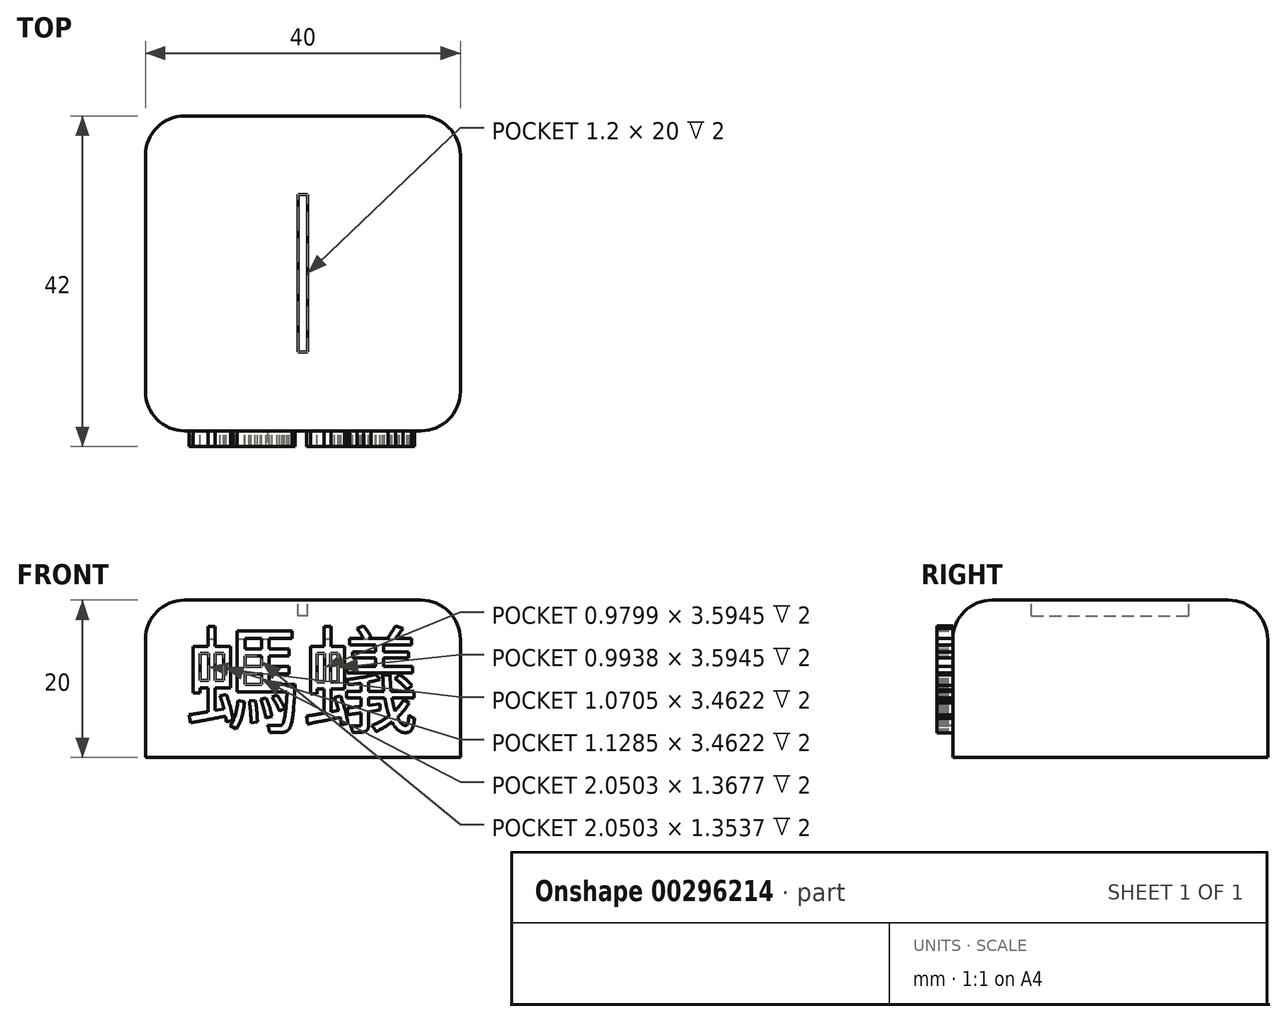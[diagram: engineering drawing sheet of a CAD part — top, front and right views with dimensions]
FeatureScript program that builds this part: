
annotation { "Feature Type Name" : "Feature", "Feature Type Description" : "" }
export const myFeature = defineFeature(function(context is Context, id is Id, definition is map)
    precondition{}
    {
        {
            var Q0;
            Q0=qCreatedBy(makeId("Top.planeOp"),FACE);
            var sketch = newSketch(context, id + "F0", { "sketchPlane" : qUnion([Q0])});
            skLineSegment(sketch, "E0.bottom", {"start": v(20, -20) * mm, "end": v(-20, -20) * mm});
            skLineSegment(sketch, "E0.top", {"start": v(20, 20) * mm, "end": v(-20, 20) * mm});
            skLineSegment(sketch, "E0.left", {"start": v(20, -20) * mm, "end": v(20, 20) * mm});
            skLineSegment(sketch, "E0.right", {"start": v(-20, -20) * mm, "end": v(-20, 20) * mm});
            skPoint(sketch, "E0.middle", {"position": v(0, 0) * mm});
            skLineSegment(sketch, "E1.bottom", {"start": v(0.6, -10) * mm, "end": v(-0.6, -10) * mm});
            skLineSegment(sketch, "E1.top", {"start": v(0.6, 10) * mm, "end": v(-0.6, 10) * mm});
            skLineSegment(sketch, "E1.left", {"start": v(0.6, -10) * mm, "end": v(0.6, 10) * mm});
            skLineSegment(sketch, "E1.right", {"start": v(-0.6, -10) * mm, "end": v(-0.6, 10) * mm});
            skSolve(sketch);
        }
        {
            var Q0;
            Q0=makeQuery(id+"F0.imprint","IMPRINT",FACE,{"disambiguationData":[TD([[makeQuery(id+"F0.imprint","IMPRINT",EDGE,{"derivedFrom":sQuery(id+"F0.wireOp",EDGE,"E0.bottom")}),-1.0]])]});
            var Q1;
            Q1=makeQuery(id+"F0.imprint","IMPRINT",FACE,{"disambiguationData":[TD([[makeQuery(id+"F0.imprint","IMPRINT",EDGE,{"derivedFrom":sQuery(id+"F0.wireOp",EDGE,"E1.bottom")}),-1.0]])]});
            extrude(context, id + "F1", {"entities" : qUnion([Q0, Q1]), "oppositeDirection" : true, "depth" : 20 * mm});
        }
        {
            var Q0;
            Q0=makeQuery(id+"F0.imprint","IMPRINT",FACE,{"disambiguationData":[TD([[makeQuery(id+"F0.imprint","IMPRINT",EDGE,{"derivedFrom":sQuery(id+"F0.wireOp",EDGE,"E1.bottom")}),-1.0]])]});
            extrude(context, id + "F2", {"entities" : qUnion([Q0]), "operationType" : NewBodyOperationType.REMOVE, "oppositeDirection" : true, "depth" : 2 * mm});
        }
        {
            var Q0;
            Q0=makeQuery(id+"F2.boolean.opBoolean","COPY",EDGE,{"derivedFrom":makeQuery(id+"F2.opExtrude","CAP_EDGE",EDGE,{"disambiguationData":[OSD([sQuery(id+"F0.wireOp",EDGE,"E1.left")])],"isStart":true})});
            var Q1;
            Q1=makeQuery(id+"F2.boolean.opBoolean","COPY",EDGE,{"derivedFrom":makeQuery(id+"F2.opExtrude","CAP_EDGE",EDGE,{"disambiguationData":[OSD([sQuery(id+"F0.wireOp",EDGE,"E1.right")])],"isStart":true})});
            var Q2;
            Q2=makeQuery(id+"F1.opExtrude","SWEPT_EDGE",EDGE,{"disambiguationData":[OSD([sQuery(id+"F0.wireOp",EDGE,"E0.bottom"),sQuery(id+"F0.wireOp",EDGE,"E0.left")])]});
            var Q3;
            Q3=makeQuery(id+"F1.opExtrude","SWEPT_EDGE",EDGE,{"disambiguationData":[OSD([sQuery(id+"F0.wireOp",EDGE,"E0.top"),sQuery(id+"F0.wireOp",EDGE,"E0.left")])]});
            var Q4;
            Q4=makeQuery(id+"F1.opExtrude","CAP_EDGE",EDGE,{"disambiguationData":[OSD([sQuery(id+"F0.wireOp",EDGE,"E0.left")])],"isStart":true});
            var Q5;
            Q5=makeQuery(id+"F1.opExtrude","SWEPT_EDGE",EDGE,{"disambiguationData":[OSD([sQuery(id+"F0.wireOp",EDGE,"E0.bottom"),sQuery(id+"F0.wireOp",EDGE,"E0.right")])]});
            var Q6;
            Q6=makeQuery(id+"F1.opExtrude","SWEPT_EDGE",EDGE,{"disambiguationData":[OSD([sQuery(id+"F0.wireOp",EDGE,"E0.top"),sQuery(id+"F0.wireOp",EDGE,"E0.right")])]});
            var Q7;
            Q7=makeQuery(id+"F1.opExtrude","CAP_EDGE",EDGE,{"disambiguationData":[OSD([sQuery(id+"F0.wireOp",EDGE,"E0.top")])],"isStart":true});
            var Q8;
            Q8=makeQuery(id+"F1.opExtrude","CAP_EDGE",EDGE,{"disambiguationData":[OSD([sQuery(id+"F0.wireOp",EDGE,"E0.right")])],"isStart":true});
            var Q9;
            Q9=makeQuery(id+"F1.opExtrude","CAP_EDGE",EDGE,{"disambiguationData":[OSD([sQuery(id+"F0.wireOp",EDGE,"E0.bottom")])],"isStart":true});
            fillet(context, id + "F3", {"entities" : qUnion([Q0, Q1, Q2, Q3, Q4, Q5, Q6, Q7, Q8, Q9]), "radius" : 5 * mm, "tangentPropagation" : true, "allowEdgeOverflow" : false});
        }
        {
            var Q0;
            Q0=makeQuery(id+"F1.opExtrude","SWEPT_FACE",FACE,{"disambiguationData":[OSD([sQuery(id+"F0.wireOp",EDGE,"E0.bottom")])]});
            var sketch = newSketch(context, id + "F4", { "sketchPlane" : qUnion([Q0])});
            skText(sketch, "E2", { "text": "螞蟻", "fontName": "NotoSansCJKtc-Regular.otf"});
            const initialGuessF4  = {"E2": [-0.015, -0.0157, 1, 0, 0.0107]};
            skSetInitialGuess(sketch, initialGuessF4);
            skSolve(sketch);
        }
        {
            var Q0;
            Q0=makeQuery(id+"F4.imprint","IMPRINT",FACE,{"disambiguationData":[TD([[makeQuery(id+"F4.imprint","IMPRINT",EDGE,{"derivedFrom":sQuery(id+"F4.wireOp",EDGE,"E2.sketch_text.stroke-111")}),1.0]])]});
            var Q1;
            {var subQ0=sQuery(id+"F4.wireOp",EDGE,"E2.sketch_text.stroke-89");Q1=makeQuery(id+"F4.imprint","IMPRINT",FACE,{"disambiguationData":[TD([[makeQuery(id+"F4.imprint","IMPRINT",EDGE,{"derivedFrom":subQ0}),1.0]])]});}
            var Q2;
            Q2=makeQuery(id+"F4.imprint","IMPRINT",FACE,{"disambiguationData":[TD([[makeQuery(id+"F4.imprint","IMPRINT",EDGE,{"derivedFrom":sQuery(id+"F4.wireOp",EDGE,"E2.sketch_text.stroke-81")}),1.0]])]});
            var Q3;
            Q3=makeQuery(id+"F4.imprint","IMPRINT",FACE,{"disambiguationData":[TD([[makeQuery(id+"F4.imprint","IMPRINT",EDGE,{"derivedFrom":sQuery(id+"F4.wireOp",EDGE,"E2.sketch_text.stroke-145")}),1.0]])]});
            var Q4;
            Q4=makeQuery(id+"F4.imprint","IMPRINT",FACE,{"disambiguationData":[TD([[makeQuery(id+"F4.imprint","IMPRINT",EDGE,{"derivedFrom":sQuery(id+"F4.wireOp",EDGE,"E2.sketch_text.stroke-115")}),1.0]])]});
            var Q5;
            {var subQ0=sQuery(id+"F4.wireOp",EDGE,"E2.sketch_text.stroke-130");Q5=makeQuery(id+"F4.imprint","IMPRINT",FACE,{"disambiguationData":[TD([[makeQuery(id+"F4.imprint","IMPRINT",EDGE,{"derivedFrom":subQ0}),1.0]])]});}
            var Q6;
            {var subQ7=sQuery(id+"F4.wireOp",EDGE,"E2.sketch_text.stroke-49");Q6=makeQuery(id+"F4.imprint","IMPRINT",FACE,{"disambiguationData":[TD([[makeQuery(id+"F4.imprint","IMPRINT",EDGE,{"derivedFrom":subQ7}),1.0]])]});}
            var Q7;
            {var subQ0=sQuery(id+"F4.wireOp",EDGE,"E2.sketch_text.stroke-17");Q7=makeQuery(id+"F4.imprint","IMPRINT",FACE,{"disambiguationData":[TD([[makeQuery(id+"F4.imprint","IMPRINT",EDGE,{"derivedFrom":subQ0}),1.0]])]});}
            extrude(context, id + "F5", {"entities" : qUnion([Q0, Q1, Q2, Q3, Q4, Q5, Q6, Q7]), "operationType" : NewBodyOperationType.ADD, "depth" : 2 * mm});
        }
        {
            var Q0;
            Q0=makeQuery(id+"F4.imprint","IMPRINT",FACE,{"disambiguationData":[TD([[makeQuery(id+"F4.imprint","IMPRINT",EDGE,{"derivedFrom":sQuery(id+"F4.wireOp",EDGE,"E2.sketch_text.stroke-0")}),1.0]])]});
            var Q1;
            Q1=makeQuery(id+"F4.imprint","IMPRINT",FACE,{"disambiguationData":[TD([[makeQuery(id+"F4.imprint","IMPRINT",EDGE,{"derivedFrom":sQuery(id+"F4.wireOp",EDGE,"E2.sketch_text.stroke-42")}),1.0]])]});
            var Q2;
            Q2=makeQuery(id+"F4.imprint","IMPRINT",FACE,{"disambiguationData":[TD([[makeQuery(id+"F4.imprint","IMPRINT",EDGE,{"derivedFrom":sQuery(id+"F4.wireOp",EDGE,"E2.sketch_text.stroke-30")}),1.0]])]});
            var Q3;
            Q3=makeQuery(id+"F4.imprint","IMPRINT",FACE,{"disambiguationData":[TD([[makeQuery(id+"F4.imprint","IMPRINT",EDGE,{"derivedFrom":sQuery(id+"F4.wireOp",EDGE,"E2.sketch_text.stroke-34")}),1.0]])]});
            var Q4;
            Q4=makeQuery(id+"F4.imprint","IMPRINT",FACE,{"disambiguationData":[TD([[makeQuery(id+"F4.imprint","IMPRINT",EDGE,{"derivedFrom":sQuery(id+"F4.wireOp",EDGE,"E2.sketch_text.stroke-38")}),1.0]])]});
            var Q5;
            Q5=makeQuery(id+"F4.imprint","IMPRINT",FACE,{"disambiguationData":[TD([[makeQuery(id+"F4.imprint","IMPRINT",EDGE,{"derivedFrom":sQuery(id+"F4.wireOp",EDGE,"E2.sketch_text.stroke-77")}),1.0]])]});
            extrude(context, id + "F6", {"entities" : qUnion([Q0, Q1, Q2, Q3, Q4, Q5]), "operationType" : NewBodyOperationType.ADD, "depth" : 2 * mm});
        }
    });
